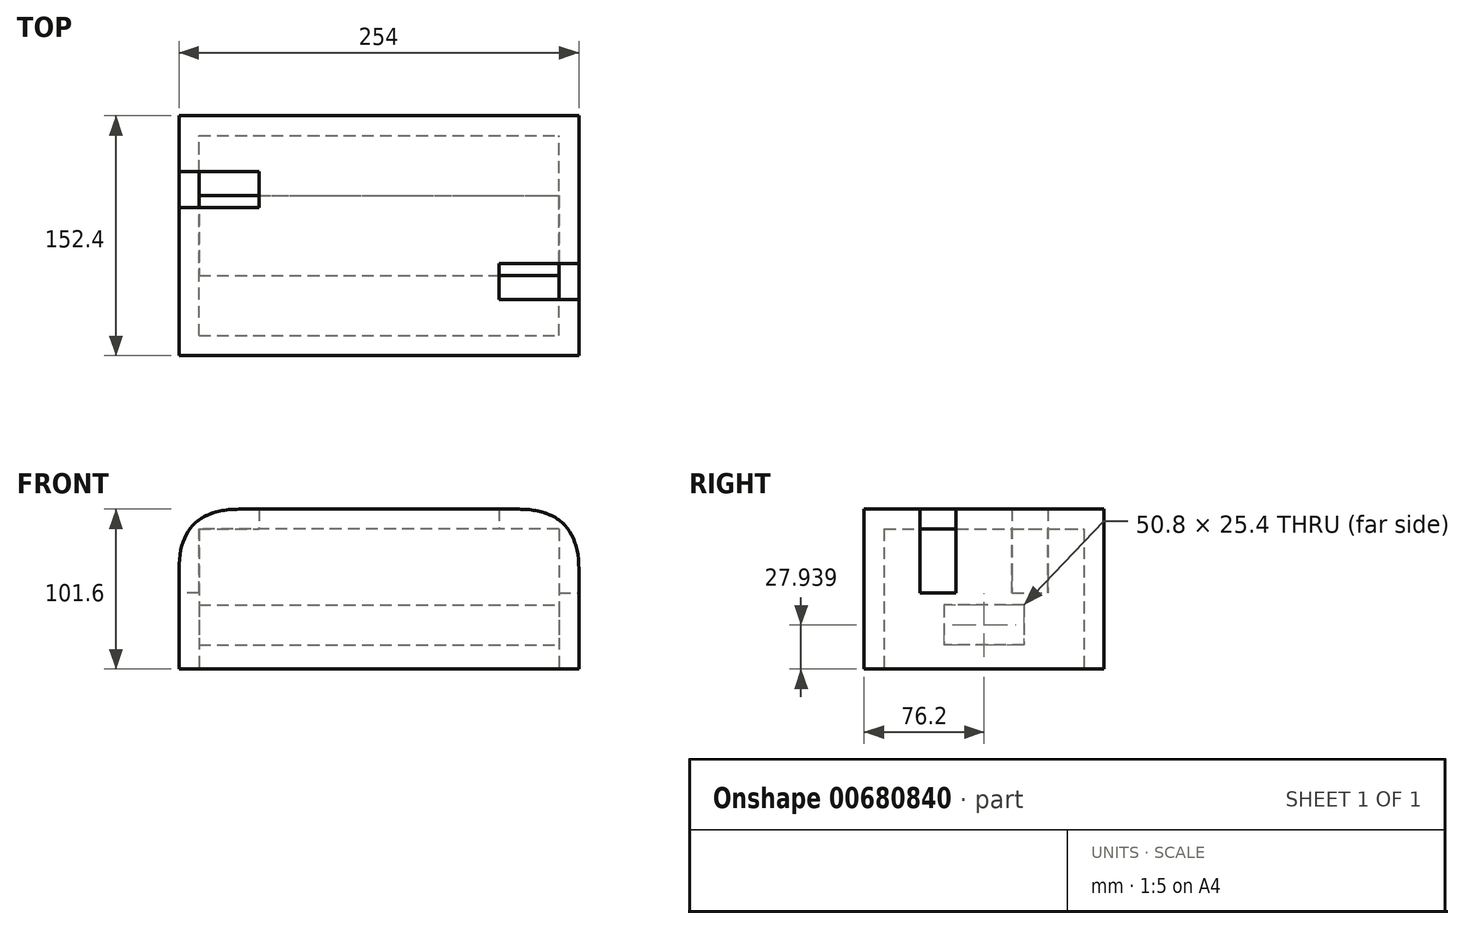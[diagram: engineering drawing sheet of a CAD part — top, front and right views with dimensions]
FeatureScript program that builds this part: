
annotation { "Feature Type Name" : "Feature", "Feature Type Description" : "" }
export const myFeature = defineFeature(function(context is Context, id is Id, definition is map)
    precondition{}
    {
        {
            var Q0;
            Q0=qCreatedBy(makeId("Front.planeOp"),FACE);
            var sketch = newSketch(context, id + "F0", { "sketchPlane" : qUnion([Q0])});
            skLineSegment(sketch, "E0.bottom", {"start": v(188.09, 89.88) * mm, "end": v(-65.91, 89.88) * mm});
            skLineSegment(sketch, "E0.top", {"start": v(188.09, -87.92) * mm, "end": v(-65.91, -87.92) * mm});
            skLineSegment(sketch, "E0.left", {"start": v(188.09, 89.88) * mm, "end": v(188.09, -87.92) * mm});
            skLineSegment(sketch, "E0.right", {"start": v(-65.91, 89.88) * mm, "end": v(-65.91, -87.92) * mm});
            skSolve(sketch);
        }
        {
            var Q0;
            Q0=makeQuery(id+"F0.imprint","IMPRINT",FACE,{"disambiguationData":[TD([[makeQuery(id+"F0.imprint","IMPRINT",EDGE,{"derivedFrom":sQuery(id+"F0.wireOp",EDGE,"E0.bottom")}),1.0]])]});
            extrude(context, id + "F1", {"entities" : qUnion([Q0]), "depth" : 152.4 * mm, "offsetDistance" : 25.4 * mm});
        }
        {
            var Q0;
            Q0=makeQuery(id+"F1.opExtrude","SWEPT_FACE",FACE,{"disambiguationData":[OSD([sQuery(id+"F0.wireOp",EDGE,"E0.top")])]});
            shell(context, id + "F2", {"entities" : qUnion([Q0]), "thickness" : 12.7 * mm});
        }
        {
            var Q0;
            Q0=makeQuery(id+"F1.opExtrude","SWEPT_EDGE",EDGE,{"disambiguationData":[OSD([sQuery(id+"F0.wireOp",EDGE,"E0.bottom"),sQuery(id+"F0.wireOp",EDGE,"E0.left")])]});
            fillet(context, id + "F3", {"entities" : qUnion([Q0]), "radius" : 38.1 * mm, "tangentPropagation" : true, "rho" : 0.5, "crossSection" : FilletCrossSection.CONIC, "allowEdgeOverflow" : false});
        }
        {
            var Q0;
            Q0=makeQuery(id+"F1.opExtrude","SWEPT_EDGE",EDGE,{"disambiguationData":[OSD([sQuery(id+"F0.wireOp",EDGE,"E0.bottom"),sQuery(id+"F0.wireOp",EDGE,"E0.right")])]});
            fillet(context, id + "F4", {"entities" : qUnion([Q0]), "radius" : 38.1 * mm, "tangentPropagation" : true, "rho" : 0.5, "crossSection" : FilletCrossSection.CONIC, "allowEdgeOverflow" : false});
        }
        {
            var Q0;
            Q0=makeQuery(id+"F1.opExtrude","SWEPT_FACE",FACE,{"disambiguationData":[OSD([sQuery(id+"F0.wireOp",EDGE,"E0.right")])]});
            var sketch = newSketch(context, id + "F5", { "sketchPlane" : qUnion([Q0])});
            skLineSegment(sketch, "E1.bottom", {"start": v(35.56, 119.86) * mm, "end": v(58.42, 119.86) * mm});
            skLineSegment(sketch, "E1.top", {"start": v(35.56, 36.54) * mm, "end": v(58.42, 36.54) * mm});
            skLineSegment(sketch, "E1.left", {"start": v(35.56, 119.86) * mm, "end": v(35.56, 36.54) * mm});
            skLineSegment(sketch, "E1.right", {"start": v(58.42, 119.86) * mm, "end": v(58.42, 36.54) * mm});
            skSolve(sketch);
        }
        {
            var Q0;
            Q0 = qSketchRegion(id + "F5", true);
            extrude(context, id + "F6", {"entities" : qUnion([Q0]), "operationType" : NewBodyOperationType.REMOVE, "oppositeDirection" : true, "depth" : 50.8 * mm, "offsetDistance" : 25.4 * mm});
        }
        {
            var Q0;
            Q0=makeQuery(id+"F1.opExtrude","SWEPT_FACE",FACE,{"disambiguationData":[OSD([sQuery(id+"F0.wireOp",EDGE,"E0.left")])]});
            var sketch = newSketch(context, id + "F7", { "sketchPlane" : qUnion([Q0])});
            skLineSegment(sketch, "E2.bottom", {"start": v(-116.84, 112.74) * mm, "end": v(-93.98, 112.74) * mm});
            skLineSegment(sketch, "E2.top", {"start": v(-116.84, 36.54) * mm, "end": v(-93.98, 36.54) * mm});
            skLineSegment(sketch, "E2.left", {"start": v(-116.84, 112.74) * mm, "end": v(-116.84, 36.54) * mm});
            skLineSegment(sketch, "E2.right", {"start": v(-93.98, 112.74) * mm, "end": v(-93.98, 36.54) * mm});
            skSolve(sketch);
        }
        {
            var Q0;
            Q0 = qSketchRegion(id + "F7", true);
            extrude(context, id + "F8", {"entities" : qUnion([Q0]), "operationType" : NewBodyOperationType.REMOVE, "oppositeDirection" : true, "depth" : 50.8 * mm, "offsetDistance" : 25.4 * mm});
        }
        {
            var Q0;
            Q0=makeQuery(id+"F2.opShell","OFFSET_FACE",FACE,{"disambiguationData":[OSD([sQuery(id+"F0.wireOp",EDGE,"E0.left")])]});
            var sketch = newSketch(context, id + "F9", { "sketchPlane" : qUnion([Q0])});
            skLineSegment(sketch, "E3.bottom", {"start": v(50.8, 28.92) * mm, "end": v(101.6, 28.92) * mm});
            skLineSegment(sketch, "E3.top", {"start": v(50.8, 3.52) * mm, "end": v(101.6, 3.52) * mm});
            skLineSegment(sketch, "E3.left", {"start": v(50.8, 28.92) * mm, "end": v(50.8, 3.52) * mm});
            skLineSegment(sketch, "E3.right", {"start": v(101.6, 28.92) * mm, "end": v(101.6, 3.52) * mm});
            skSolve(sketch);
        }
        {
            var Q0;
            Q0 = qSketchRegion(id + "F9", true);
            extrude(context, id + "F10", {"entities" : qUnion([Q0]), "operationType" : NewBodyOperationType.ADD, "depth" : 233.68 * mm, "offsetDistance" : 25.4 * mm});
        }
        {
            var Q0;
            Q0=makeQuery(id+"F1.opExtrude","CAP_FACE",FACE,{"disambiguationData":[OSD([sQuery(id+"F0.wireOp",EDGE,"E0.bottom"),sQuery(id+"F0.wireOp",EDGE,"E0.top"),sQuery(id+"F0.wireOp",EDGE,"E0.left"),sQuery(id+"F0.wireOp",EDGE,"E0.right")])],"isStart":false});
            var sketch = newSketch(context, id + "F11", { "sketchPlane" : qUnion([Q0])});
            skLineSegment(sketch, "E4.bottom", {"start": v(-74.81, -11.72) * mm, "end": v(220.59, -11.72) * mm});
            skLineSegment(sketch, "E4.top", {"start": v(-74.81, -87.92) * mm, "end": v(220.59, -87.92) * mm});
            skLineSegment(sketch, "E4.left", {"start": v(-74.81, -11.72) * mm, "end": v(-74.81, -87.92) * mm});
            skLineSegment(sketch, "E4.right", {"start": v(220.59, -11.72) * mm, "end": v(220.59, -87.92) * mm});
            skSolve(sketch);
        }
        {
            var Q0;
            {var subQ0=sQuery(id+"F11.wireOp",EDGE,"E4.bottom");var subQ1=makeQuery(id+"F1.opExtrude","CAP_EDGE",EDGE,{"disambiguationData":[OSD([sQuery(id+"F0.wireOp",EDGE,"E0.right")])],"isStart":false});var subQ2=makeQuery(id+"F11.imprint","INTERSECT",VERTEX,{"derivedFrom":[subQ1,subQ0]});Q0=makeQuery(id+"F11.imprint","IMPRINT",FACE,{"disambiguationData":[TD([[makeQuery(id+"F11.imprint","IMPRINT",EDGE,{"disambiguationData":[TD([[subQ2,-1.0]])],"derivedFrom":subQ0}),-1.0]])]});}
            extrude(context, id + "F12", {"entities" : qUnion([Q0]), "operationType" : NewBodyOperationType.REMOVE, "oppositeDirection" : true, "depth" : 180.34 * mm, "offsetDistance" : 25.4 * mm});
        }
    });
